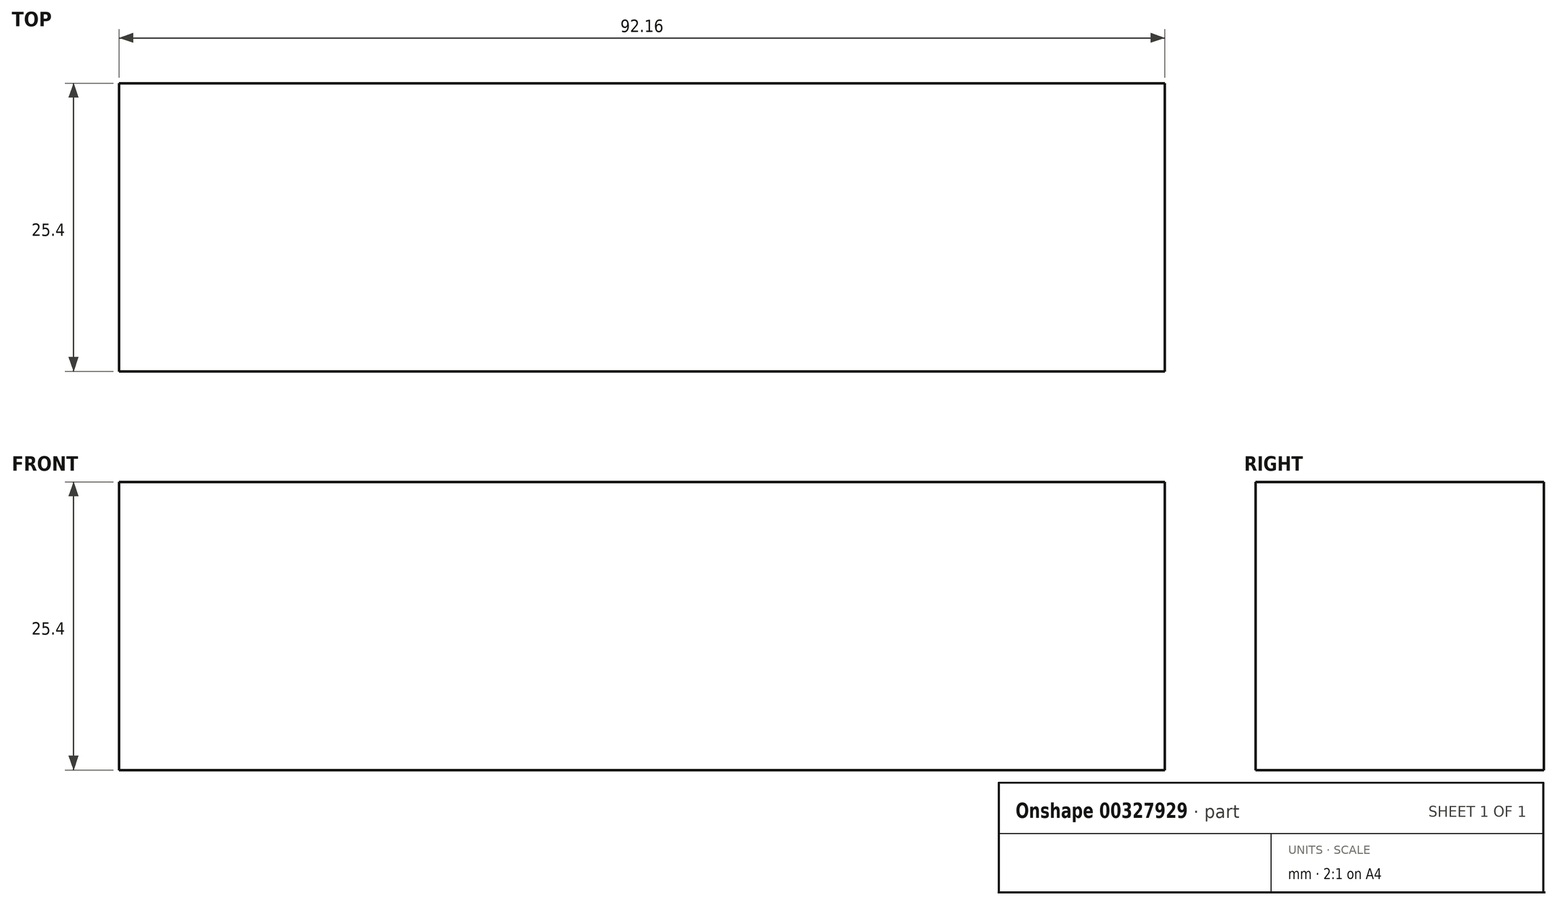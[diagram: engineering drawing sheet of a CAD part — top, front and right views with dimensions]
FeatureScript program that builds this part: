
annotation { "Feature Type Name" : "Feature", "Feature Type Description" : "" }
export const myFeature = defineFeature(function(context is Context, id is Id, definition is map)
    precondition{}
    {
        {
            var Q0;
            Q0=qCreatedBy(makeId("Front.planeOp"),FACE);
            var sketch = newSketch(context, id + "F0", { "sketchPlane" : qUnion([Q0])});
            skLineSegment(sketch, "E0.bottom", {"start": v(-40.72, 33.86) * mm, "end": v(51.44, 33.86) * mm});
            skLineSegment(sketch, "E0.top", {"start": v(-40.72, -53.14) * mm, "end": v(51.44, -53.14) * mm});
            skLineSegment(sketch, "E0.left", {"start": v(-40.72, 33.86) * mm, "end": v(-40.72, -53.14) * mm});
            skLineSegment(sketch, "E0.right", {"start": v(51.44, 33.86) * mm, "end": v(51.44, -53.14) * mm});
            skSolve(sketch);
        }
        {
            var Q0;
            Q0=sQuery(id+"F0.wireOp",EDGE,"E0.bottom");
            extrude(context, id + "F1", {"bodyType" : ToolBodyType.SURFACE, "surfaceEntities" : qUnion([Q0]), "oppositeDirection" : true, "depth" : 25.4 * mm});
        }
        {
            var Q0;
            Q0=makeQuery(id+"F1.opExtrude","SWEPT_FACE",FACE,{"disambiguationData":[OSD([sQuery(id+"F0.wireOp",EDGE,"E0.bottom")])]});
            extrude(context, id + "F2", {"entities" : qUnion([Q0]), "depth" : 25.4 * mm});
        }
    });
